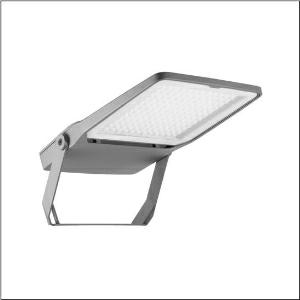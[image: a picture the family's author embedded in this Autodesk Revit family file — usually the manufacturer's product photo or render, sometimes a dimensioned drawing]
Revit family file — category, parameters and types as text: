
# Revit family: floodlight_fl_20_midi___pl43_5xa7682d2a1ac_5ef8
name_source: partatom
category: Lighting Fixtures
units: mm (PartAtom-declared; Revit-internal decimal feet)

## family parameters
Cut with Voids When Loaded = No
Host = Face
Light Source = No
Part Type = Normal
Room Calculation Point = No
Round Connector Dimension = Use Diameter
Shared = No

## types (1)
- --- (1 x LED 4000K / CRI = 70 (unbekannt), 19080 lm, 4000K)
    Apparent Load = 142 VA
    CIE Flux Codes = 32 74 99 100 100
    Color Rendering = 70
    Color Temperature = 4000K
    Default Elevation = 1800 mm
    Description = Floodlight FL 20 midi, floodlight, primary light control with lens, of plastic, primary optical cover: protective disc, of toughened safety glass, transparent, light distribution: PL43, light emission: direct distribution, primary light characteristic: asymmetric, installation type: surface-mounted, LED, High Power LED, rated luminous flux: 19.080lm, luminous efficacy: 134lm/W, light colour: 740, colour temperature: 4000K, control gear: ECG Plus, control: flexible luminous flux parameterisation, time-dependent luminous flux control, digital communication interface, power reduction, overheat protection, electronic power reduction, with terminal, 5-pole, max. 2.5mm², mains connection: 220..240V, AC, 50/60Hz, rated input power: 142W, LED unit, of diecast aluminium, powder-coated, Siteco® metallic grey (DB 702S), corrosivity category C5 mid according to DIN EN ISO 12944, incl. 1x M20 cable gland for cable Ø 6.5..12mm, length: 654mm, width: 450mm, height: 76mm, housing frame, of diecast aluminium, powder-coated, Siteco® metallic grey (DB 702S), mounting bracket, of steel, powder-coated, Siteco® metallic grey (DB 702S), DALI, protection rating (complete): IP66, insulation class (complete): insulation class II (safety insulation), certification: CE, ENEC, VDE, protection symbol: D, permissible operating ambient temperature: -40..+40°C, permissible operating ambient temperature for outdoor applications: -40..+50°C, standard: DIN EN 12944, packaging unit: 1 piece

Light Distribution: PL43
    Height = 76 mm
    Lamp = 1 x LED 4000K / CRI >= 70 (unbekannt)
    Lamp Light Flux = 19080 lm
    Lamp count = 1
    Length = 672 mm
    Luminous efficacy = 134 lm/W
    Manufacturer = Siteco
    ModVariant = No
    Model = 5XA7682D2A1AC
    Mounting Place = Wall
    Mounting Type = Surface mounted
    Number of Poles = 1
    OnlyDefault = Yes
    Power Factor = 1
    Product Name = Floodlight FL 20 midi | PL43
    Product group = floodlight | wall mounted
    ProductGroupID = 2001
    Protection Class = Protection class II
    Protection Degree = IP 66
    RLX_Detail_Level = 1
    RLX_Emergency_Light_Flux = 0 lm
    RLX_Emergency_Type = 0
    RLX_Emergency_Type_DB = No
    RlxData = <blob elided: 97553 chars, md5=d007d72f>
    Socket = socket
    Standby Power = 0 W
    System Light Flux = 19080 lm
    System Power = 142 W
    Type Comments = factory setting: luminous flux: 100 % | dim-lin: 254 | 489 mA
    Type Image = l_1005943.jpg
    URL = http://relux.com
    VarID = @adj_148077
    Voltage = 0 V
    Weight = 0.00 kg
    Width = 450 mm

## geometry (parser evidence)
native form markers: Blend x4, Sweep x13
no freeform markers — native parametric forms only
